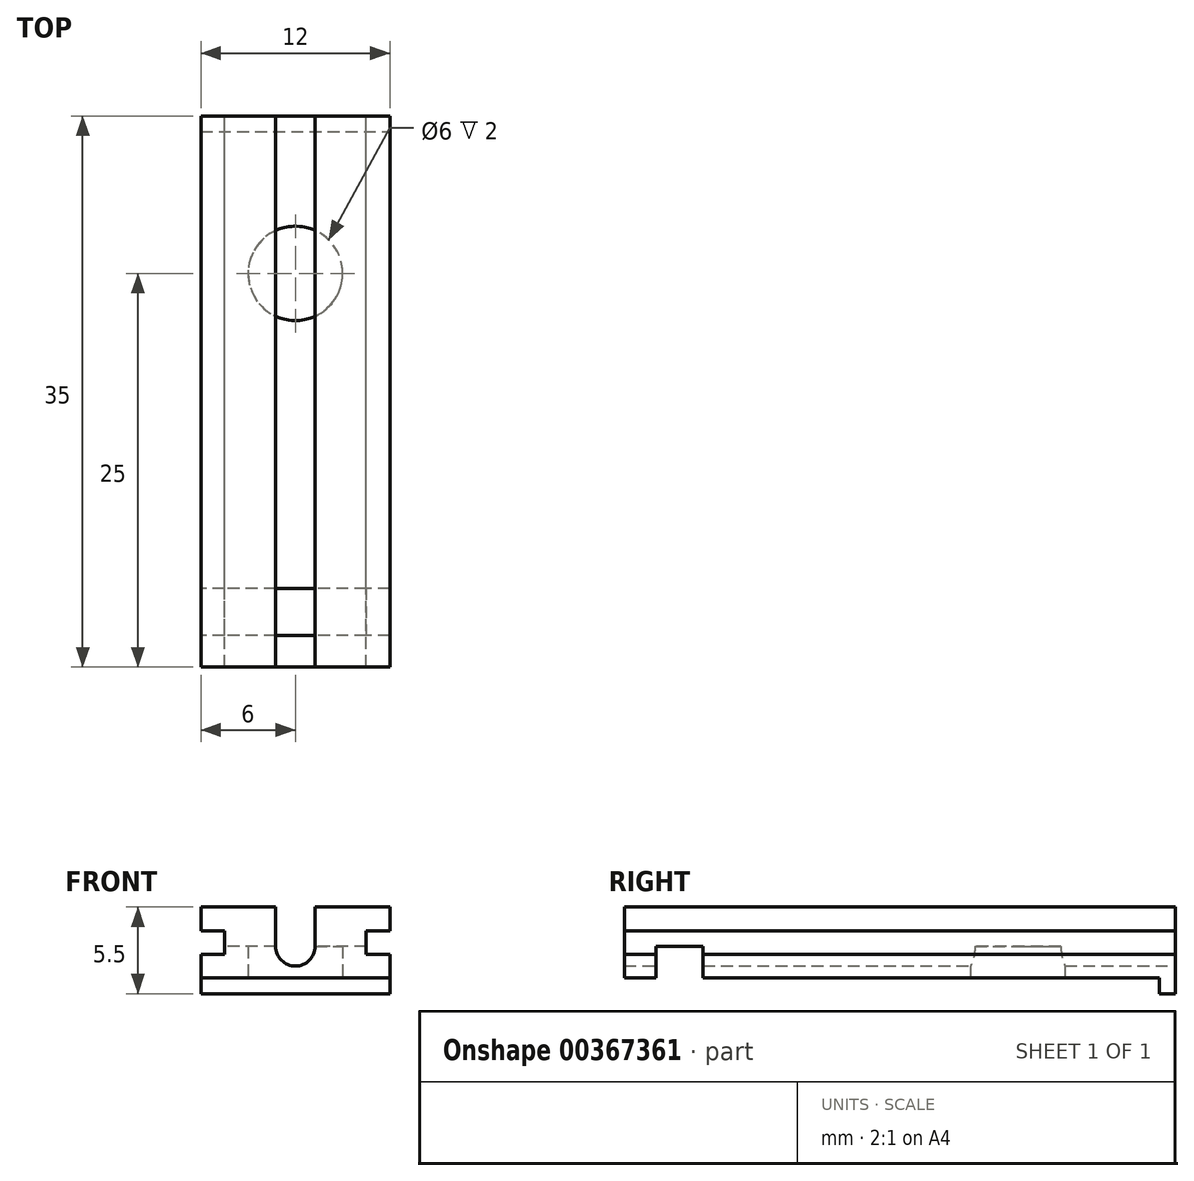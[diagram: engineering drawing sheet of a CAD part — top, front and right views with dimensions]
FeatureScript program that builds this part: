
annotation { "Feature Type Name" : "Feature", "Feature Type Description" : "" }
export const myFeature = defineFeature(function(context is Context, id is Id, definition is map)
    precondition{}
    {
        {
            var Q0;
            Q0=qCreatedBy(makeId("Front.planeOp"),FACE);
            var sketch = newSketch(context, id + "F0", { "sketchPlane" : qUnion([Q0])});
            skLineSegment(sketch, "E0", {"start": v(0, 0) * mm, "end": v(6, 0) * mm});
            skLineSegment(sketch, "E1", {"start": v(6, 0) * mm, "end": v(6, 1.5) * mm});
            skLineSegment(sketch, "E2", {"start": v(6, 1.5) * mm, "end": v(4.5, 1.5) * mm});
            skLineSegment(sketch, "E3", {"start": v(4.5, 1.5) * mm, "end": v(4.5, 3) * mm});
            skLineSegment(sketch, "E4", {"start": v(4.5, 3) * mm, "end": v(6, 3) * mm});
            skLineSegment(sketch, "E5", {"start": v(6, 3) * mm, "end": v(6, 4.5) * mm});
            skLineSegment(sketch, "E6", {"start": v(6, 4.5) * mm, "end": v(1.25, 4.5) * mm});
            skLineSegment(sketch, "E7", {"start": v(1.25, 4.5) * mm, "end": v(1.25, 2) * mm});
            skArc(sketch, "E8", {"start": v(1.25, 2) * mm, "mid": v(0.88, 1.12) * mm, "end": v(0, 0.75) * mm});
            skLineSegment(sketch, "E9", {"start": v(0, 0.75) * mm, "end": v(0, 0) * mm});
            skLineSegment(sketch, "E10.bottom", {"start": v(6, 0) * mm, "end": v(-6, 0) * mm});
            skLineSegment(sketch, "E10.top", {"start": v(6, -1) * mm, "end": v(-6, -1) * mm});
            skLineSegment(sketch, "E10.left", {"start": v(6, 0) * mm, "end": v(6, -1) * mm});
            skLineSegment(sketch, "E10.right", {"start": v(-6, 0) * mm, "end": v(-6, -1) * mm});
            skSolve(sketch);
        }
        {
            var Q0;
            Q0=makeQuery(id+"F0.imprint","IMPRINT",FACE,{"disambiguationData":[TD([[makeQuery(id+"F0.imprint","IMPRINT",EDGE,{"derivedFrom":sQuery(id+"F0.wireOp",EDGE,"E0")}),1.0]])]});
            var Q1;
            {var subQ0=sQuery(id+"F0.wireOp",EDGE,"E1");Q1=makeQuery(id+"F0.imprint","IMPRINT",FACE,{"disambiguationData":[TD([[makeQuery(id+"F0.imprint","IMPRINT",EDGE,{"derivedFrom":subQ0}),1.0]])]});}
            extrude(context, id + "F1", {"entities" : qUnion([Q0, Q1]), "depth" : 35 * mm});
        }
        {
            var Q0;
            Q0=makeQuery(id+"F1.opExtrude","SWEPT_BODY",BODY,{"disambiguationData":[OSD([sQuery(id+"F0.wireOp",EDGE,"E0"),sQuery(id+"F0.wireOp",EDGE,"E1"),sQuery(id+"F0.wireOp",EDGE,"E2"),sQuery(id+"F0.wireOp",EDGE,"E3"),sQuery(id+"F0.wireOp",EDGE,"E4"),sQuery(id+"F0.wireOp",EDGE,"E5"),sQuery(id+"F0.wireOp",EDGE,"E6"),sQuery(id+"F0.wireOp",EDGE,"E7"),sQuery(id+"F0.wireOp",EDGE,"E8"),sQuery(id+"F0.wireOp",EDGE,"E9")])]});
            var Q1;
            Q1=qCreatedBy(makeId("Right.planeOp"),FACE);
            mirror(context, id + "F2", {"operationType" : NewBodyOperationType.ADD, "entities" : qUnion([Q0]), "mirrorPlane" : qUnion([Q1])});
        }
        {
            var Q0;
            Q0=makeQuery(id+"F0.imprint","IMPRINT",FACE,{"disambiguationData":[TD([[makeQuery(id+"F0.imprint","IMPRINT",EDGE,{"derivedFrom":sQuery(id+"F0.wireOp",EDGE,"E10.top")}),-1.0]])]});
            extrude(context, id + "F3", {"entities" : qUnion([Q0]), "operationType" : NewBodyOperationType.ADD, "depth" : 1 * mm});
        }
        {
            var Q0;
            Q0=qCreatedBy(makeId("Right.planeOp"),FACE);
            var sketch = newSketch(context, id + "F4", { "sketchPlane" : qUnion([Q0])});
            skLineSegment(sketch, "E11.bottom", {"start": v(-30, 0) * mm, "end": v(-33, 0) * mm});
            skLineSegment(sketch, "E11.top", {"start": v(-30, 2) * mm, "end": v(-33, 2) * mm});
            skLineSegment(sketch, "E11.left", {"start": v(-30, 0) * mm, "end": v(-30, 2) * mm});
            skLineSegment(sketch, "E11.right", {"start": v(-33, 0) * mm, "end": v(-33, 2) * mm});
            skSolve(sketch);
        }
        {
            var Q0;
            Q0=makeQuery(id+"F4.imprint","IMPRINT",FACE,{"disambiguationData":[TD([[makeQuery(id+"F4.imprint","IMPRINT",EDGE,{"derivedFrom":sQuery(id+"F4.wireOp",EDGE,"E11.bottom")}),-1.0]])]});
            extrude(context, id + "F5", {"entities" : qUnion([Q0]), "operationType" : NewBodyOperationType.REMOVE, "endBound" : BoundingType.SYMMETRIC, "depth" : 50 * mm});
        }
        {
            var Q0;
            Q0=qCreatedBy(makeId("Top.planeOp"),FACE);
            var sketch = newSketch(context, id + "F6", { "sketchPlane" : qUnion([Q0])});
            skPoint(sketch, "E12", {"position": v(0, -10) * mm});
            skLineSegment(sketch, "E13", {"start": v(0, -10) * mm, "end": v(0, 0) * mm});
            skSolve(sketch);
        }
        {
            var Q0;
            Q0=sQuery(id+"F6.wireOp",VERTEX,"E12");
            var Q1;
            Q1=makeQuery(id+"F1.opExtrude","SWEPT_BODY",BODY,{"disambiguationData":[OSD([sQuery(id+"F0.wireOp",EDGE,"E1"),sQuery(id+"F0.wireOp",EDGE,"E2"),sQuery(id+"F0.wireOp",EDGE,"E3"),sQuery(id+"F0.wireOp",EDGE,"E4"),sQuery(id+"F0.wireOp",EDGE,"E5"),sQuery(id+"F0.wireOp",EDGE,"E6"),sQuery(id+"F0.wireOp",EDGE,"E7"),sQuery(id+"F0.wireOp",EDGE,"E8"),sQuery(id+"F0.wireOp",EDGE,"E9"),sQuery(id+"F0.wireOp",EDGE,"E10.bottom")])]});
            hole(context, id + "F7", {"style" : HoleStyle.C_BORE, "endStyle" : HoleEndStyle.THROUGH, "oppositeDirection" : true, "holeDiameter" : 2.5 * mm, "cBoreDiameter" : 6 * mm, "cBoreDepth" : 2 * mm, "isTappedThrough" : true, "tappedDepth" : 12 * mm, "tapClearance" : 3, "startFromSketch" : true, "locations" : qUnion([Q0]), "scope" : qUnion([Q1])});
        }
    });
